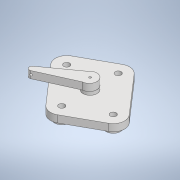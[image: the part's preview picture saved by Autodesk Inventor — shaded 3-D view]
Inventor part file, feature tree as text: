
AUTODESK INVENTOR PART (.ipt)
format: ipt  version: 2021 (Build 250183000, 183)  size: 249,344 bytes
history: native  units: mm
features: extrude x6, sketch x5, fillet x2, other x1
ambient origin geometry x8: Origin, YZ Plane, XZ Plane, XY Plane, X Axis, Y Axis, Z Axis, Center Point
bodies: Body1 (feature_tree)
feature tree (14):
  other  "솔리드1"
  extrude  "돌출1"  Depth=4.2mm
  extrude  "돌출2"  Depth=47.0mm
  fillet  "모깎기1"  Radius=14.0mm
  extrude  "돌출3"  Depth=40.0mm
  sketch  "스케치4"
  extrude  "돌출4"  Depth=15.0mm
  extrude  "돌출5"  Depth=5.0mm TaperAngle=0.0deg
  fillet  "모깎기2"  Radius=8.0mm
  extrude  "돌출6"  Depth=3.0mm
  sketch  "스케치1"
  sketch  "스케치2"
  sketch  "스케치3"
  sketch  "스케치5"
